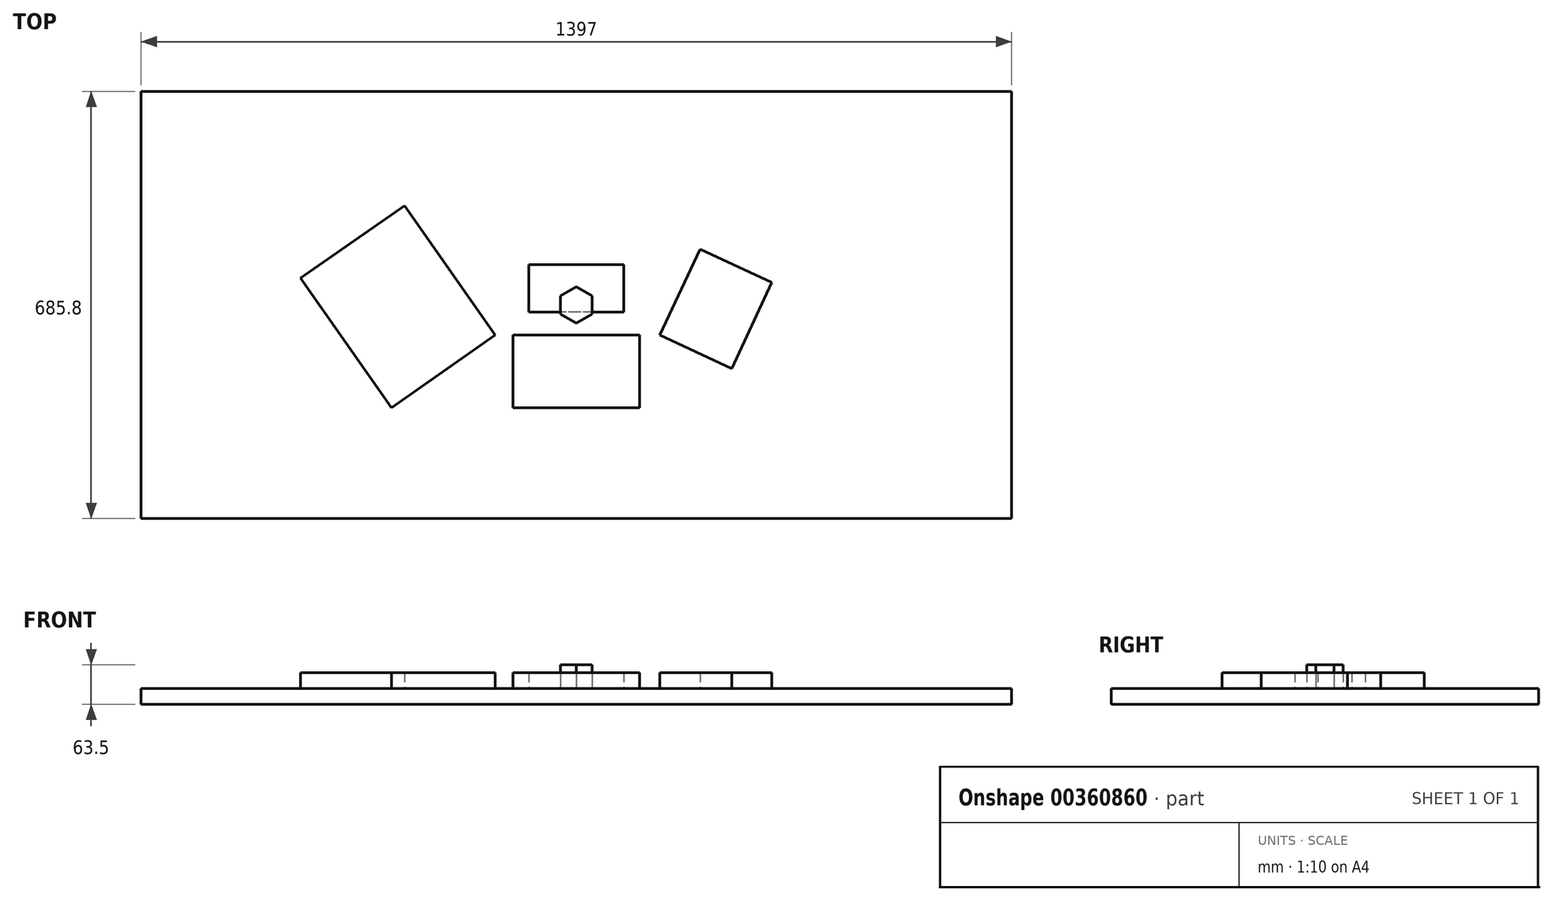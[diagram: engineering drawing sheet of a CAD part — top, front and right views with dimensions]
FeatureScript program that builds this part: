
annotation { "Feature Type Name" : "Feature", "Feature Type Description" : "" }
export const myFeature = defineFeature(function(context is Context, id is Id, definition is map)
    precondition{}
    {
        {
            var Q0;
            Q0=qCreatedBy(makeId("Top.planeOp"),FACE);
            var sketch = newSketch(context, id + "F0", { "sketchPlane" : qUnion([Q0])});
            skLineSegment(sketch, "E0.bottom", {"start": v(698.5, 342.9) * mm, "end": v(-698.5, 342.9) * mm});
            skLineSegment(sketch, "E0.top", {"start": v(698.5, -342.9) * mm, "end": v(-698.5, -342.9) * mm});
            skLineSegment(sketch, "E0.left", {"start": v(698.5, 342.9) * mm, "end": v(698.5, -342.9) * mm});
            skLineSegment(sketch, "E0.right", {"start": v(-698.5, 342.9) * mm, "end": v(-698.5, -342.9) * mm});
            skPoint(sketch, "E0.middle", {"position": v(0, 0) * mm});
            skSolve(sketch);
        }
        {
            var Q0;
            Q0 = qSketchRegion(id + "F0", true);
            extrude(context, id + "F1", {"entities" : qUnion([Q0]), "depth" : 25.4 * mm});
        }
        {
            var Q0;
            Q0=makeQuery(id+"F1.opExtrude","CAP_FACE",FACE,{"disambiguationData":[OSD([sQuery(id+"F0.wireOp",EDGE,"E0.bottom"),sQuery(id+"F0.wireOp",EDGE,"E0.top"),sQuery(id+"F0.wireOp",EDGE,"E0.left"),sQuery(id+"F0.wireOp",EDGE,"E0.right")])],"isStart":false});
            var sketch = newSketch(context, id + "F2", { "sketchPlane" : qUnion([Q0])});
            skLineSegment(sketch, "E1.bottom", {"start": v(101.6, -48.55) * mm, "end": v(-101.6, -48.55) * mm});
            skLineSegment(sketch, "E1.top", {"start": v(101.6, -165.1) * mm, "end": v(-101.6, -165.1) * mm});
            skLineSegment(sketch, "E1.left", {"start": v(101.6, -48.55) * mm, "end": v(101.6, -165.1) * mm});
            skLineSegment(sketch, "E1.right", {"start": v(-101.6, -48.55) * mm, "end": v(-101.6, -165.1) * mm});
            skPoint(sketch, "E1.middle", {"position": v(0, -106.82) * mm});
            skLineSegment(sketch, "E2.bottom", {"start": v(-130.46, -48.65) * mm, "end": v(-296.98, -165.1) * mm});
            skLineSegment(sketch, "E2.top", {"start": v(-276.02, 159.5) * mm, "end": v(-442.54, 43.05) * mm});
            skLineSegment(sketch, "E2.left", {"start": v(-130.46, -48.65) * mm, "end": v(-276.02, 159.5) * mm});
            skLineSegment(sketch, "E2.right", {"start": v(-296.98, -165.1) * mm, "end": v(-442.54, 43.05) * mm});
            skPoint(sketch, "E2.middle", {"position": v(-286.5, -2.8) * mm});
            skLineSegment(sketch, "E3.bottom", {"start": v(198.47, 89.47) * mm, "end": v(313.57, 35.8) * mm});
            skLineSegment(sketch, "E3.top", {"start": v(134.06, -48.65) * mm, "end": v(249.17, -102.32) * mm});
            skLineSegment(sketch, "E3.left", {"start": v(198.47, 89.47) * mm, "end": v(134.06, -48.65) * mm});
            skLineSegment(sketch, "E3.right", {"start": v(313.57, 35.8) * mm, "end": v(249.17, -102.32) * mm});
            skPoint(sketch, "E4", {"position": v(220.12, -7.96) * mm});
            skPoint(sketch, "E4.positionSnap0", {"position": v(191.61, -75.48) * mm});
            skPoint(sketch, "E4.positionSnap1", {"position": v(166.27, 20.41) * mm});
            skLineSegment(sketch, "E5.bottom", {"start": v(76.2, -11.57) * mm, "end": v(-76.2, -11.57) * mm});
            skLineSegment(sketch, "E5.top", {"start": v(76.2, 64.63) * mm, "end": v(-76.2, 64.63) * mm});
            skLineSegment(sketch, "E5.left", {"start": v(76.2, -11.57) * mm, "end": v(76.2, 64.63) * mm});
            skLineSegment(sketch, "E5.right", {"start": v(-76.2, -11.57) * mm, "end": v(-76.2, 64.63) * mm});
            skPoint(sketch, "E5.middle", {"position": v(0, 26.53) * mm});
            skPoint(sketch, "E6.0.midPoint", {"position": v(25.4, 0) * mm});
            skSolve(sketch);
        }
        {
            var Q0;
            Q0 = qSketchRegion(id + "F2", true);
            extrude(context, id + "F3", {"entities" : qUnion([Q0]), "depth" : 25.4 * mm});
        }
        {
            var Q0;
            Q0=makeQuery(id+"F1.opExtrude","CAP_FACE",FACE,{"disambiguationData":[OSD([sQuery(id+"F0.wireOp",EDGE,"E0.bottom"),sQuery(id+"F0.wireOp",EDGE,"E0.top"),sQuery(id+"F0.wireOp",EDGE,"E0.left"),sQuery(id+"F0.wireOp",EDGE,"E0.right")])],"isStart":false});
            var sketch = newSketch(context, id + "F4", { "sketchPlane" : qUnion([Q0])});
            skCircle(sketch, "E7.cCircle", {"center": v(0, 0) * mm, "radius": 25.4 * mm, "construction": true});
            skLineSegment(sketch, "E7.0", {"start": v(25.4, 14.66) * mm, "end": v(25.4, -14.66) * mm});
            skLineSegment(sketch, "E7.1", {"start": v(25.4, -14.66) * mm, "end": v(0, -29.33) * mm});
            skLineSegment(sketch, "E7.2", {"start": v(0, -29.33) * mm, "end": v(-25.4, -14.66) * mm});
            skLineSegment(sketch, "E7.3", {"start": v(-25.4, -14.66) * mm, "end": v(-25.4, 14.66) * mm});
            skLineSegment(sketch, "E7.4", {"start": v(-25.4, 14.66) * mm, "end": v(0, 29.33) * mm});
            skLineSegment(sketch, "E7.5", {"start": v(0, 29.33) * mm, "end": v(25.4, 14.66) * mm});
            skPoint(sketch, "E7.0.midPoint", {"position": v(25.4, 0) * mm});
            skSolve(sketch);
        }
        {
            var Q0;
            Q0 = qSketchRegion(id + "F4", true);
            extrude(context, id + "F5", {"entities" : qUnion([Q0]), "depth" : 38.1 * mm});
        }
    });
